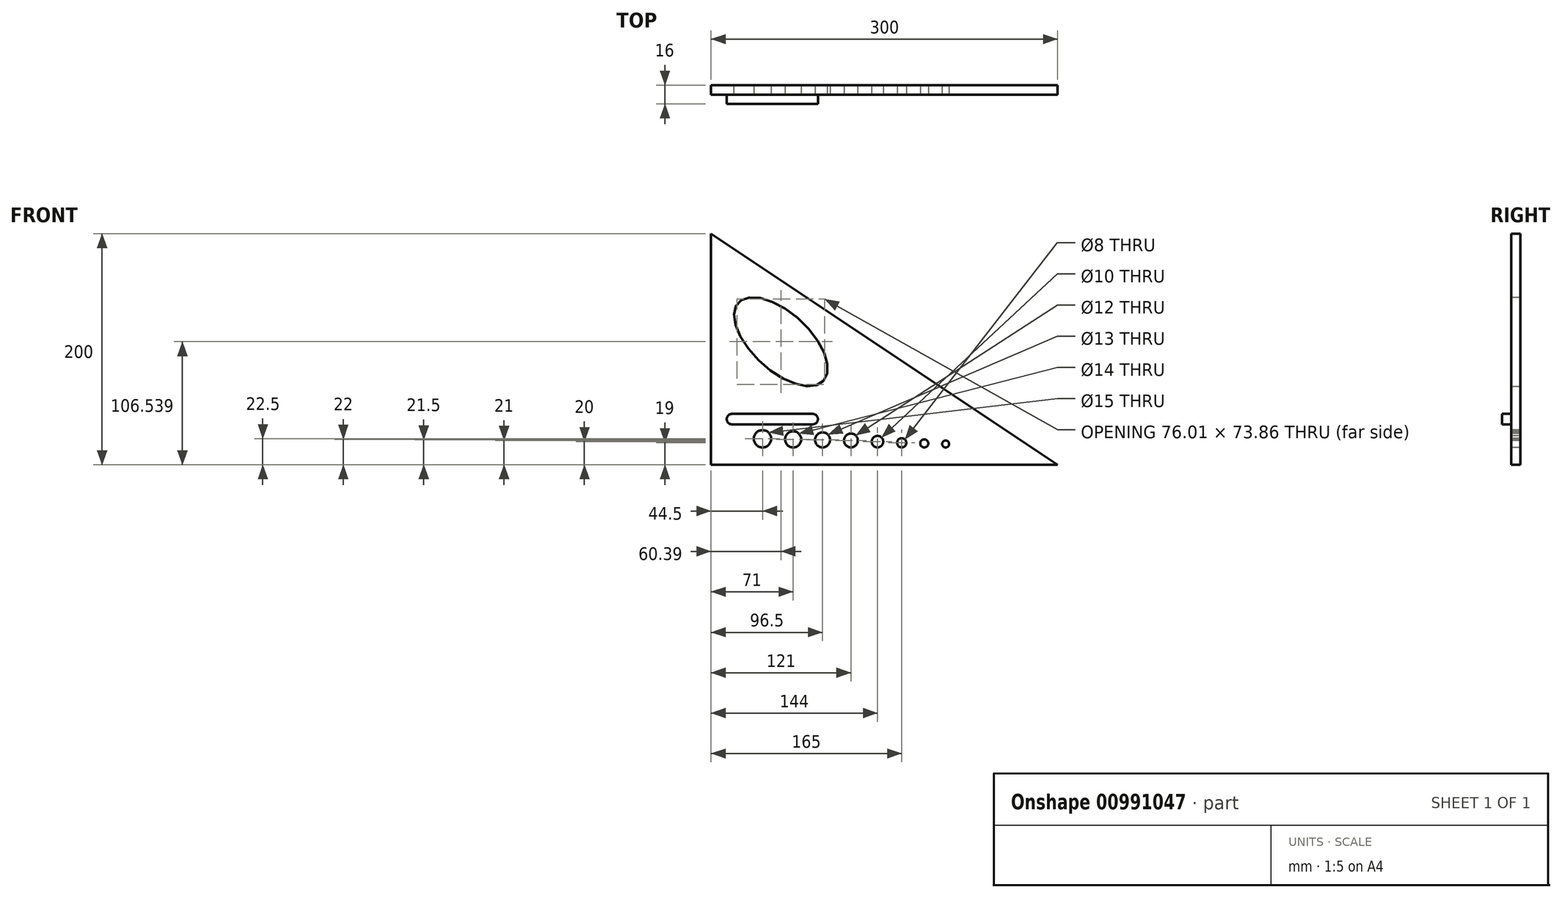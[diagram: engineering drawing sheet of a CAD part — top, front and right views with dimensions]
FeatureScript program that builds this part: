
annotation { "Feature Type Name" : "Feature", "Feature Type Description" : "" }
export const myFeature = defineFeature(function(context is Context, id is Id, definition is map)
    precondition{}
    {
        {
            var Q0;
            Q0=qCreatedBy(makeId("Front.planeOp"),FACE);
            var sketch = newSketch(context, id + "F0", { "sketchPlane" : qUnion([Q0])});
            skLineSegment(sketch, "E0", {"start": v(0, 0) * mm, "end": v(0, 200) * mm});
            skLineSegment(sketch, "E1", {"start": v(0, 0) * mm, "end": v(300, 0) * mm});
            skLineSegment(sketch, "E2", {"start": v(300, 0) * mm, "end": v(0, 200) * mm});
            skSolve(sketch);
        }
        {
            var Q0;
            Q0=makeQuery(id+"F0.imprint","IMPRINT",FACE,{"disambiguationData":[TD([[makeQuery(id+"F0.imprint","IMPRINT",EDGE,{"derivedFrom":sQuery(id+"F0.wireOp",EDGE,"E0")}),-1.0]])]});
            extrude(context, id + "F1", {"entities" : qUnion([Q0]), "depth" : 8 * mm, "offsetDistance" : 25 * mm});
        }
        {
            var Q0;
            Q0=makeQuery(id+"F1.opExtrude","CAP_FACE",FACE,{"disambiguationData":[OSD([sQuery(id+"F0.wireOp",EDGE,"E0"),sQuery(id+"F0.wireOp",EDGE,"E1"),sQuery(id+"F0.wireOp",EDGE,"E2")])],"isStart":false});
            var sketch = newSketch(context, id + "F2", { "sketchPlane" : qUnion([Q0])});
            skLineSegment(sketch, "E3", {"start": v(0, 0) * mm, "end": v(0, 15) * mm});
            skLineSegment(sketch, "E4", {"start": v(0, 15) * mm, "end": v(327.06, 15) * mm});
            skLineSegment(sketch, "E5", {"start": v(0, 15) * mm, "end": v(96.5, 15) * mm});
            skLineSegment(sketch, "E6", {"start": v(96.5, 15) * mm, "end": v(96.5, 21.5) * mm});
            skLineSegment(sketch, "E7", {"start": v(96.5, 15) * mm, "end": v(121, 15) * mm});
            skLineSegment(sketch, "E8", {"start": v(121, 15) * mm, "end": v(121, 21) * mm});
            skLineSegment(sketch, "E9", {"start": v(121, 15) * mm, "end": v(144, 15) * mm});
            skLineSegment(sketch, "E10", {"start": v(144, 15) * mm, "end": v(144, 20) * mm});
            skLineSegment(sketch, "E11", {"start": v(144, 15) * mm, "end": v(165, 15) * mm});
            skLineSegment(sketch, "E12", {"start": v(165, 15) * mm, "end": v(165, 19) * mm});
            skLineSegment(sketch, "E13", {"start": v(165, 15) * mm, "end": v(184.5, 15) * mm});
            skLineSegment(sketch, "E14", {"start": v(184.5, 15) * mm, "end": v(184.5, 18.5) * mm});
            skLineSegment(sketch, "E15", {"start": v(184.5, 15) * mm, "end": v(203, 15) * mm});
            skLineSegment(sketch, "E16", {"start": v(203, 15) * mm, "end": v(203, 18) * mm});
            skCircle(sketch, "E17", {"center": v(96.5, 21.5) * mm, "radius": 6.5 * mm});
            skCircle(sketch, "E18", {"center": v(121, 21) * mm, "radius": 6 * mm});
            skCircle(sketch, "E19", {"center": v(144, 20) * mm, "radius": 5 * mm});
            skCircle(sketch, "E20", {"center": v(165, 19) * mm, "radius": 4 * mm});
            skCircle(sketch, "E21", {"center": v(184.5, 18.5) * mm, "radius": 3.5 * mm});
            skCircle(sketch, "E22", {"center": v(203, 18) * mm, "radius": 3 * mm});
            skSolve(sketch);
        }
        {
            var Q0;
            Q0=makeQuery(id+"F2.imprint","IMPRINT",FACE,{"disambiguationData":[TD([[makeQuery(id+"F2.imprint","IMPRINT",EDGE,{"derivedFrom":sQuery(id+"F2.wireOp",EDGE,"E17")}),1.0]])]});
            var Q1;
            Q1=makeQuery(id+"F2.imprint","IMPRINT",FACE,{"disambiguationData":[TD([[makeQuery(id+"F2.imprint","IMPRINT",EDGE,{"derivedFrom":sQuery(id+"F2.wireOp",EDGE,"E18")}),1.0]])]});
            var Q2;
            Q2=makeQuery(id+"F2.imprint","IMPRINT",FACE,{"disambiguationData":[TD([[makeQuery(id+"F2.imprint","IMPRINT",EDGE,{"derivedFrom":sQuery(id+"F2.wireOp",EDGE,"E19")}),1.0]])]});
            var Q3;
            Q3=makeQuery(id+"F2.imprint","IMPRINT",FACE,{"disambiguationData":[TD([[makeQuery(id+"F2.imprint","IMPRINT",EDGE,{"derivedFrom":sQuery(id+"F2.wireOp",EDGE,"E20")}),1.0]])]});
            var Q4;
            Q4=makeQuery(id+"F2.imprint","IMPRINT",FACE,{"disambiguationData":[TD([[makeQuery(id+"F2.imprint","IMPRINT",EDGE,{"derivedFrom":sQuery(id+"F2.wireOp",EDGE,"E21")}),1.0]])]});
            var Q5;
            Q5=makeQuery(id+"F2.imprint","IMPRINT",FACE,{"disambiguationData":[TD([[makeQuery(id+"F2.imprint","IMPRINT",EDGE,{"derivedFrom":sQuery(id+"F2.wireOp",EDGE,"E22")}),1.0]])]});
            extrude(context, id + "F3", {"entities" : qUnion([Q0, Q1, Q2, Q3, Q4, Q5]), "operationType" : NewBodyOperationType.REMOVE, "oppositeDirection" : true, "depth" : 25 * mm, "offsetDistance" : 25 * mm});
        }
        {
            var Q0;
            Q0=makeQuery(id+"F1.opExtrude","CAP_FACE",FACE,{"disambiguationData":[OSD([sQuery(id+"F0.wireOp",EDGE,"E0"),sQuery(id+"F0.wireOp",EDGE,"E1"),sQuery(id+"F0.wireOp",EDGE,"E2")])],"isStart":false});
            var sketch = newSketch(context, id + "F4", { "sketchPlane" : qUnion([Q0])});
            skLineSegment(sketch, "E23", {"start": v(0, 0) * mm, "end": v(0, 35) * mm});
            skLineSegment(sketch, "E24", {"start": v(0, 35) * mm, "end": v(15, 35) * mm});
            skLineSegment(sketch, "E25", {"start": v(15, 35) * mm, "end": v(15, 44) * mm});
            skLineSegment(sketch, "E26", {"start": v(15, 44) * mm, "end": v(91, 44) * mm});
            skLineSegment(sketch, "E27", {"start": v(91, 44) * mm, "end": v(91, 35) * mm});
            skLineSegment(sketch, "E28", {"start": v(91, 35) * mm, "end": v(15, 35) * mm});
            skLineSegment(sketch, "E29", {"start": v(15, 39.5) * mm, "end": v(18, 39.5) * mm});
            skLineSegment(sketch, "E30", {"start": v(91, 39.5) * mm, "end": v(88, 39.5) * mm});
            skCircle(sketch, "E31", {"center": v(18, 39.5) * mm, "radius": 4.5 * mm});
            skCircle(sketch, "E32", {"center": v(88, 39.5) * mm, "radius": 4.5 * mm});
            skSolve(sketch);
        }
        {
            var Q0;
            {var subQ0=sQuery(id+"F4.wireOp",EDGE,"E31");var subQ1=sQuery(id+"F4.wireOp",EDGE,"E26");var subQ2=makeQuery(id+"F4.imprint","INTERSECT",VERTEX,{"derivedFrom":[subQ1,subQ0]});Q0=makeQuery(id+"F4.imprint","IMPRINT",FACE,{"disambiguationData":[TD([[makeQuery(id+"F4.imprint","IMPRINT",EDGE,{"disambiguationData":[TD([[subQ2,-1.0]])],"derivedFrom":subQ1}),-1.0]])]});}
            var Q1;
            {var subQ1=sQuery(id+"F4.wireOp",EDGE,"E25");var subQ4=makeQuery(id+"F4.imprint","IMPRINT",VERTEX,{"derivedFrom":subQ1});Q1=makeQuery(id+"F4.imprint","IMPRINT",FACE,{"disambiguationData":[TD([[makeQuery(id+"F4.imprint","IMPRINT",EDGE,{"disambiguationData":[TD([[subQ4,1.0]])],"derivedFrom":subQ1}),-1.0]])]});}
            var Q2;
            {var subQ0=sQuery(id+"F4.wireOp",EDGE,"E25");var subQ1=makeQuery(id+"F4.imprint","IMPRINT",VERTEX,{"derivedFrom":subQ0});Q2=makeQuery(id+"F4.imprint","IMPRINT",FACE,{"disambiguationData":[TD([[makeQuery(id+"F4.imprint","IMPRINT",EDGE,{"disambiguationData":[TD([[subQ1,1.0]])],"derivedFrom":subQ0}),1.0]])]});}
            var Q3;
            {var subQ3=sQuery(id+"F4.wireOp",EDGE,"E27");var subQ4=makeQuery(id+"F4.imprint","IMPRINT",VERTEX,{"derivedFrom":subQ3});Q3=makeQuery(id+"F4.imprint","IMPRINT",FACE,{"disambiguationData":[TD([[makeQuery(id+"F4.imprint","IMPRINT",EDGE,{"disambiguationData":[TD([[subQ4,1.0]])],"derivedFrom":subQ3}),-1.0]])]});}
            var Q4;
            {var subQ0=sQuery(id+"F4.wireOp",EDGE,"E27");var subQ1=makeQuery(id+"F4.imprint","IMPRINT",VERTEX,{"derivedFrom":subQ0});Q4=makeQuery(id+"F4.imprint","IMPRINT",FACE,{"disambiguationData":[TD([[makeQuery(id+"F4.imprint","IMPRINT",EDGE,{"disambiguationData":[TD([[subQ1,1.0]])],"derivedFrom":subQ0}),1.0]])]});}
            extrude(context, id + "F5", {"entities" : qUnion([Q0, Q1, Q2, Q3, Q4]), "operationType" : NewBodyOperationType.ADD, "depth" : 8 * mm, "offsetDistance" : 25 * mm});
        }
        {
            var Q0;
            Q0=makeQuery(id+"F1.opExtrude","CAP_FACE",FACE,{"disambiguationData":[OSD([sQuery(id+"F0.wireOp",EDGE,"E0"),sQuery(id+"F0.wireOp",EDGE,"E1"),sQuery(id+"F0.wireOp",EDGE,"E2")])],"isStart":false});
            var sketch = newSketch(context, id + "F6", { "sketchPlane" : qUnion([Q0])});
            skEllipse(sketch, "E33", {"center": v(60.39, 106.54) * mm, "majorRadius": 50 * mm, "minorRadius": 25 * mm, "majorAxis": v(0.74, -0.68)});
            skSolve(sketch);
        }
        {
            var Q0;
            Q0=makeQuery(id+"F6.imprint","IMPRINT",FACE,{"disambiguationData":[TD([[makeQuery(id+"F6.imprint","IMPRINT",EDGE,{"derivedFrom":sQuery(id+"F6.wireOp",EDGE,"E33")}),1.0]])]});
            extrude(context, id + "F7", {"entities" : qUnion([Q0]), "operationType" : NewBodyOperationType.REMOVE, "oppositeDirection" : true, "depth" : 25 * mm, "offsetDistance" : 25 * mm});
        }
        {
            var Q0;
            Q0=makeQuery(id+"F1.opExtrude","CAP_FACE",FACE,{"disambiguationData":[OSD([sQuery(id+"F0.wireOp",EDGE,"E0"),sQuery(id+"F0.wireOp",EDGE,"E1"),sQuery(id+"F0.wireOp",EDGE,"E2")])],"isStart":false});
            var sketch = newSketch(context, id + "F8", { "sketchPlane" : qUnion([Q0])});
            skLineSegment(sketch, "E34", {"start": v(0, 0) * mm, "end": v(0, 15) * mm});
            skLineSegment(sketch, "E35", {"start": v(0, 15) * mm, "end": v(110.56, 15) * mm});
            skLineSegment(sketch, "E36", {"start": v(96.5, 21.5) * mm, "end": v(71, 21.5) * mm});
            skLineSegment(sketch, "E37", {"start": v(71, 21.5) * mm, "end": v(71, 7.64) * mm});
            skLineSegment(sketch, "E38", {"start": v(71, 15) * mm, "end": v(71, 22) * mm});
            skPoint(sketch, "E38.startSnap0", {"position": v(71, 14.57) * mm});
            skCircle(sketch, "E39", {"center": v(71, 22) * mm, "radius": 7 * mm});
            skSolve(sketch);
        }
        {
            var Q0;
            {var subQ0=sQuery(id+"F8.wireOp",EDGE,"E38");var subQ1=sQuery(id+"F8.wireOp",EDGE,"E36");var subQ2=makeQuery(id+"F8.imprint","INTERSECT",VERTEX,{"derivedFrom":[subQ1,subQ0]});Q0=makeQuery(id+"F8.imprint","IMPRINT",FACE,{"disambiguationData":[TD([[makeQuery(id+"F8.imprint","IMPRINT",EDGE,{"disambiguationData":[TD([[subQ2,1.0]])],"derivedFrom":subQ1}),1.0]])]});}
            var Q1;
            {var subQ0=sQuery(id+"F8.wireOp",EDGE,"E38");var subQ1=sQuery(id+"F8.wireOp",EDGE,"E36");var subQ2=makeQuery(id+"F8.imprint","INTERSECT",VERTEX,{"derivedFrom":[subQ1,subQ0]});Q1=makeQuery(id+"F8.imprint","IMPRINT",FACE,{"disambiguationData":[TD([[makeQuery(id+"F8.imprint","IMPRINT",EDGE,{"disambiguationData":[TD([[subQ2,1.0]])],"derivedFrom":subQ1}),-1.0]])]});}
            extrude(context, id + "F9", {"entities" : qUnion([Q0, Q1]), "operationType" : NewBodyOperationType.REMOVE, "oppositeDirection" : true, "depth" : 25 * mm, "offsetDistance" : 25 * mm});
        }
        {
            var Q0;
            Q0=makeQuery(id+"F1.opExtrude","CAP_FACE",FACE,{"disambiguationData":[OSD([sQuery(id+"F0.wireOp",EDGE,"E0"),sQuery(id+"F0.wireOp",EDGE,"E1"),sQuery(id+"F0.wireOp",EDGE,"E2")])],"isStart":false});
            var sketch = newSketch(context, id + "F10", { "sketchPlane" : qUnion([Q0])});
            skLineSegment(sketch, "E40", {"start": v(0, 0) * mm, "end": v(0, 15) * mm});
            skLineSegment(sketch, "E41", {"start": v(0, 15) * mm, "end": v(96.5, 15) * mm});
            skLineSegment(sketch, "E42", {"start": v(71, 22) * mm, "end": v(71, 15) * mm});
            skLineSegment(sketch, "E43", {"start": v(71, 15) * mm, "end": v(44.5, 15) * mm});
            skLineSegment(sketch, "E44", {"start": v(44.5, 15) * mm, "end": v(44.5, 22.5) * mm});
            skCircle(sketch, "E45", {"center": v(44.5, 22.5) * mm, "radius": 7.5 * mm});
            skSolve(sketch);
        }
        {
            var Q0;
            Q0=makeQuery(id+"F10.imprint","IMPRINT",FACE,{"disambiguationData":[TD([[makeQuery(id+"F10.imprint","IMPRINT",EDGE,{"derivedFrom":sQuery(id+"F10.wireOp",EDGE,"E45")}),1.0]])]});
            extrude(context, id + "F11", {"entities" : qUnion([Q0]), "operationType" : NewBodyOperationType.REMOVE, "oppositeDirection" : true, "depth" : 25 * mm, "offsetDistance" : 25 * mm});
        }
    });
